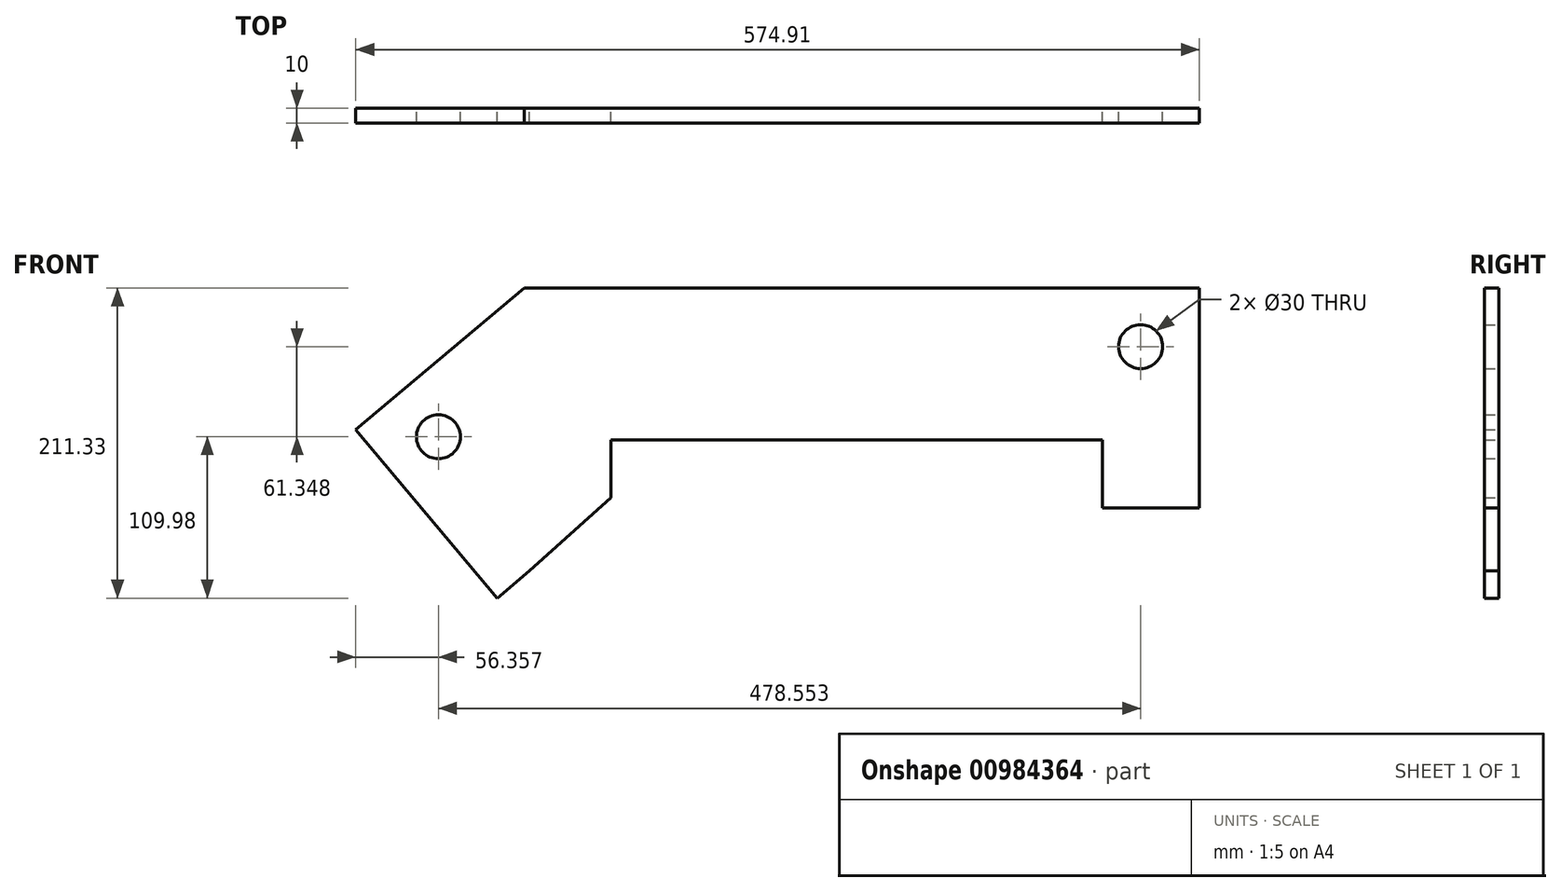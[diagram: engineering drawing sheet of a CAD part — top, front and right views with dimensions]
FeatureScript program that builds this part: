
annotation { "Feature Type Name" : "Feature", "Feature Type Description" : "" }
export const myFeature = defineFeature(function(context is Context, id is Id, definition is map)
    precondition{}
    {
        {
            var Q0;
            Q0=qCreatedBy(makeId("Front.planeOp"),FACE);
            var sketch = newSketch(context, id + "F0", { "sketchPlane" : qUnion([Q0])});
            skLineSegment(sketch, "E0.top", {"start": v(230, 96.42) * mm, "end": v(-230, 96.42) * mm});
            skLineSegment(sketch, "E0.left", {"start": v(230, -53.58) * mm, "end": v(230, 96.42) * mm});
            skPoint(sketch, "E0.middle", {"position": v(0, 0) * mm});
            skPoint(sketch, "E1", {"position": v(-230, -96.42) * mm});
            skPoint(sketch, "E2", {"position": v(-230, 96.42) * mm});
            skLineSegment(sketch, "E3", {"start": v(-230, 96.42) * mm, "end": v(-344.9, 0) * mm});
            skLineSegment(sketch, "E4", {"start": v(-344.9, 0) * mm, "end": v(-248.49, -114.9) * mm});
            skLineSegment(sketch, "E5", {"start": v(-248.49, -114.9) * mm, "end": v(-226.45, -96.42) * mm});
            skCircle(sketch, "E6", {"center": v(190, 56.42) * mm, "radius": 15 * mm});
            skCircle(sketch, "E7", {"center": v(-288.55, -4.93) * mm, "radius": 15 * mm});
            skLineSegment(sketch, "E8", {"start": v(-226.45, -96.42) * mm, "end": v(-170.9, -46.42) * mm});
            skLineSegment(sketch, "E9", {"start": v(230, 96.42) * mm, "end": v(230, -53.58) * mm});
            skLineSegment(sketch, "E10", {"start": v(230, -53.58) * mm, "end": v(163.92, -53.58) * mm});
            skLineSegment(sketch, "E11", {"start": v(163.92, -53.58) * mm, "end": v(163.92, -7.16) * mm});
            skLineSegment(sketch, "E12", {"start": v(163.92, -7.16) * mm, "end": v(-171.15, -7.16) * mm});
            skLineSegment(sketch, "E13", {"start": v(-171.15, -7.16) * mm, "end": v(-170.9, -46.42) * mm});
            skPoint(sketch, "E14.start.orphan", {"position": v(150, -96.42) * mm});
            skPoint(sketch, "E15.orphan", {"position": v(230, -96.42) * mm});
            skSolve(sketch);
        }
        {
            var Q0;
            Q0=qSketchRegion(id+"F0",true);
            var Q1;
            Q1=makeQuery(id+"F0.imprint","IMPRINT",FACE,{"disambiguationData":[TD([[makeQuery(id+"F0.imprint","IMPRINT",EDGE,{"derivedFrom":sQuery(id+"F0.wireOp",EDGE,"E0.top")}),1.0]])]});
            extrude(context, id + "F1", {"entities" : qUnion([Q0, Q1]), "depth" : 10 * mm, "offsetDistance" : 25 * mm});
        }
    });
